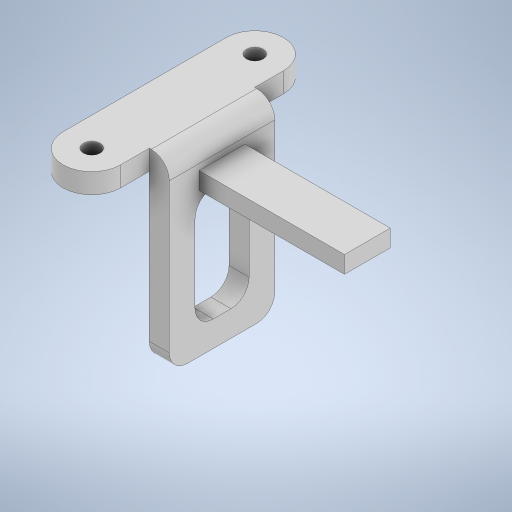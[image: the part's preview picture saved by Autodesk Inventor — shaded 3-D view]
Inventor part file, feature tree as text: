
AUTODESK INVENTOR PART (.ipt)
format: ipt  version: 2023 (Build 270158000, 158)  size: 668,160 bytes
history: native  units: in
note: dims shown in document units (in); Inventor stores cm internally (conversion verified against a paired STEP export)
features: extrude x4, sketch x4, fillet x1
ambient origin geometry x8: Origin, YZ Plane, XZ Plane, XY Plane, X Axis, Y Axis, Z Axis, Center Point
bodies: Solid1 (feature_tree)
feature tree (9):
  extrude  "Extrusion1"  Depth=0.116in
  sketch  "Sketch2"  dims[d3=0.395in d4=0.395in]
  extrude  "Extrusion4"  Depth=0.395in
  extrude  "Extrusion5"  Depth=0.1378in
  fillet  "Fillet3"  Radius=0.198in
  extrude  "Extrusion6"  Depth=1.0in
  sketch  "Sketch1"  dims[d0=0.116in d2=0.116in]
  sketch  "Sketch4"  dims[d5=0.1378in d6=0.0in d7=0.198in d8=0.198in]
  sketch  "Sketch5"  dims[d9=1.138in d10=0.25in d14=0.25in d17=0.125in d23=0.25in d25=0.125in d26=0.1378in d27=0.0in d29=0.1378in d30=0.0in d31=0.125in d36=1.0in d37=0.0in]
